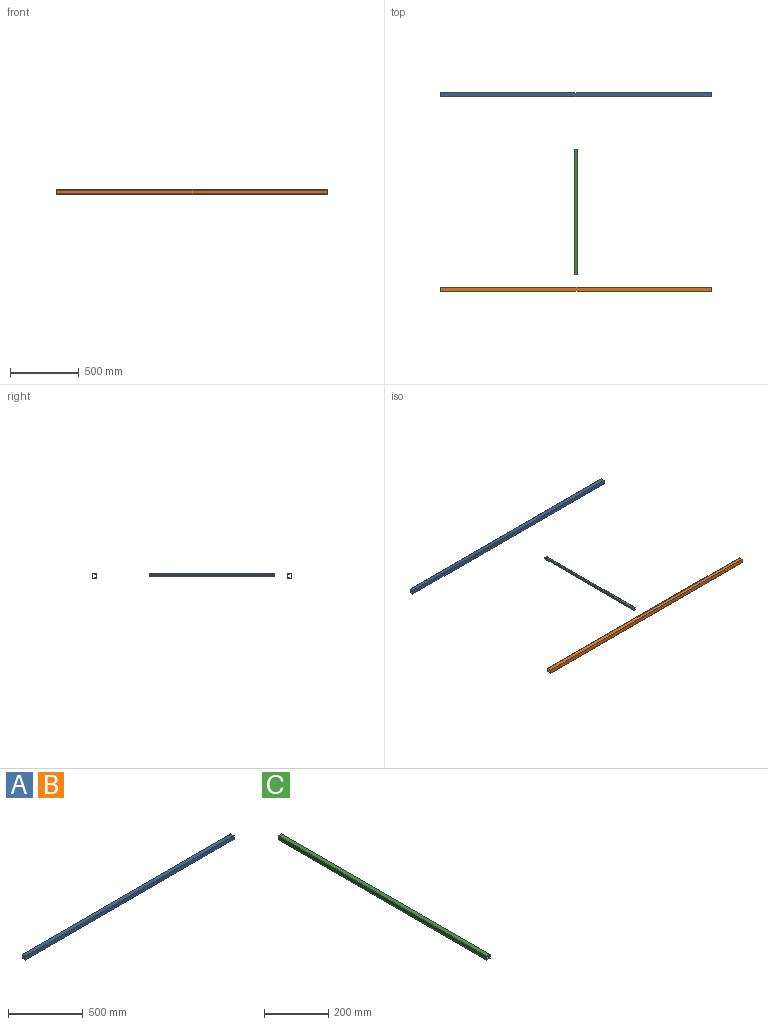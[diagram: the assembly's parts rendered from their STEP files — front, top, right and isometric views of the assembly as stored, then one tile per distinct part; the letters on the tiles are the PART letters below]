
ASSEMBLY  parts=3 mates=3
PART A: 10 faces, bbox 1970x30x30 mm
  f0: plane 1970x30mm, normal (0,0,1), area 59100mm2, adj f1,f7,f8,f9
  f1: plane 1970x30mm, normal (0,-1,0), area 59100mm2, adj f0,f2,f8,f9
  f2: plane 1970x30mm, normal (0,0,-1), area 59100mm2, adj f1,f7,f8,f9
  f3: plane 1970x26mm, normal (0,0,1), area 51220mm2, adj f4,f6,f8,f9
  f4: plane 1970x26mm, normal (0,1,0), area 51220mm2, adj f3,f5,f8,f9
  f5: plane 1970x26mm, normal (0,0,-1), area 51220mm2, adj f4,f6,f8,f9
  f6: plane 1970x26mm, normal (0,-1,0), area 51220mm2, adj f3,f5,f8,f9
  f7: plane 1970x30mm, normal (0,1,0), area 59100mm2, adj f0,f2,f8,f9
  f8: plane 30x30mm, normal (-1,0,0), area 224mm2, adj f0,f1,f2,f3,f4,f5,f6,f7
  f9: plane 30x30mm, normal (1,0,0), area 224mm2, adj f0,f1,f2,f3,f4,f5,f6,f7
PART B: same geometry as A
PART C: 10 faces, bbox 15x915x15 mm
  f0: plane 915x12.6mm, normal (-1,0,0), area 11529mm2, adj f1,f7,f8,f9
  f1: plane 915x12.6mm, normal (0,0,1), area 11529mm2, adj f0,f2,f8,f9
  f2: plane 915x12.6mm, normal (1,0,0), area 11529mm2, adj f1,f7,f8,f9
  f3: plane 915x15mm, normal (1,0,0), area 13725mm2, adj f4,f6,f8,f9
  f4: plane 915x15mm, normal (0,0,1), area 13725mm2, adj f3,f5,f8,f9
  f5: plane 915x15mm, normal (-1,0,0), area 13725mm2, adj f4,f6,f8,f9
  f6: plane 915x15mm, normal (0,0,-1), area 13725mm2, adj f3,f5,f8,f9
  f7: plane 915x12.6mm, normal (0,0,-1), area 11529mm2, adj f0,f2,f8,f9
  f8: plane 15x15mm, normal (0,-1,0), area 66.2mm2, adj f0,f1,f2,f3,f4,f5,f6,f7
  f9: plane 15x15mm, normal (0,1,0), area 66.2mm2, adj f0,f1,f2,f3,f4,f5,f6,f7
PLACE A t=(531.15,1542.49,7.53)mm
PLACE B t=(531.15,127.49,7.53)mm
PLACE C t=(-453.85,1149.99,11.03)mm
MATE planar B.f0 <-> A.f0  axis (0,0,1) through (-453.85,130.49,18.53)mm
MATE planar A.f8 <-> B.f8  axis (-1,0,0) through (-1438.85,1558.49,3.53)mm
MATE planar C.f4 <-> A.f0  axis (0,0,1) through (-453.85,692.49,18.53)mm
